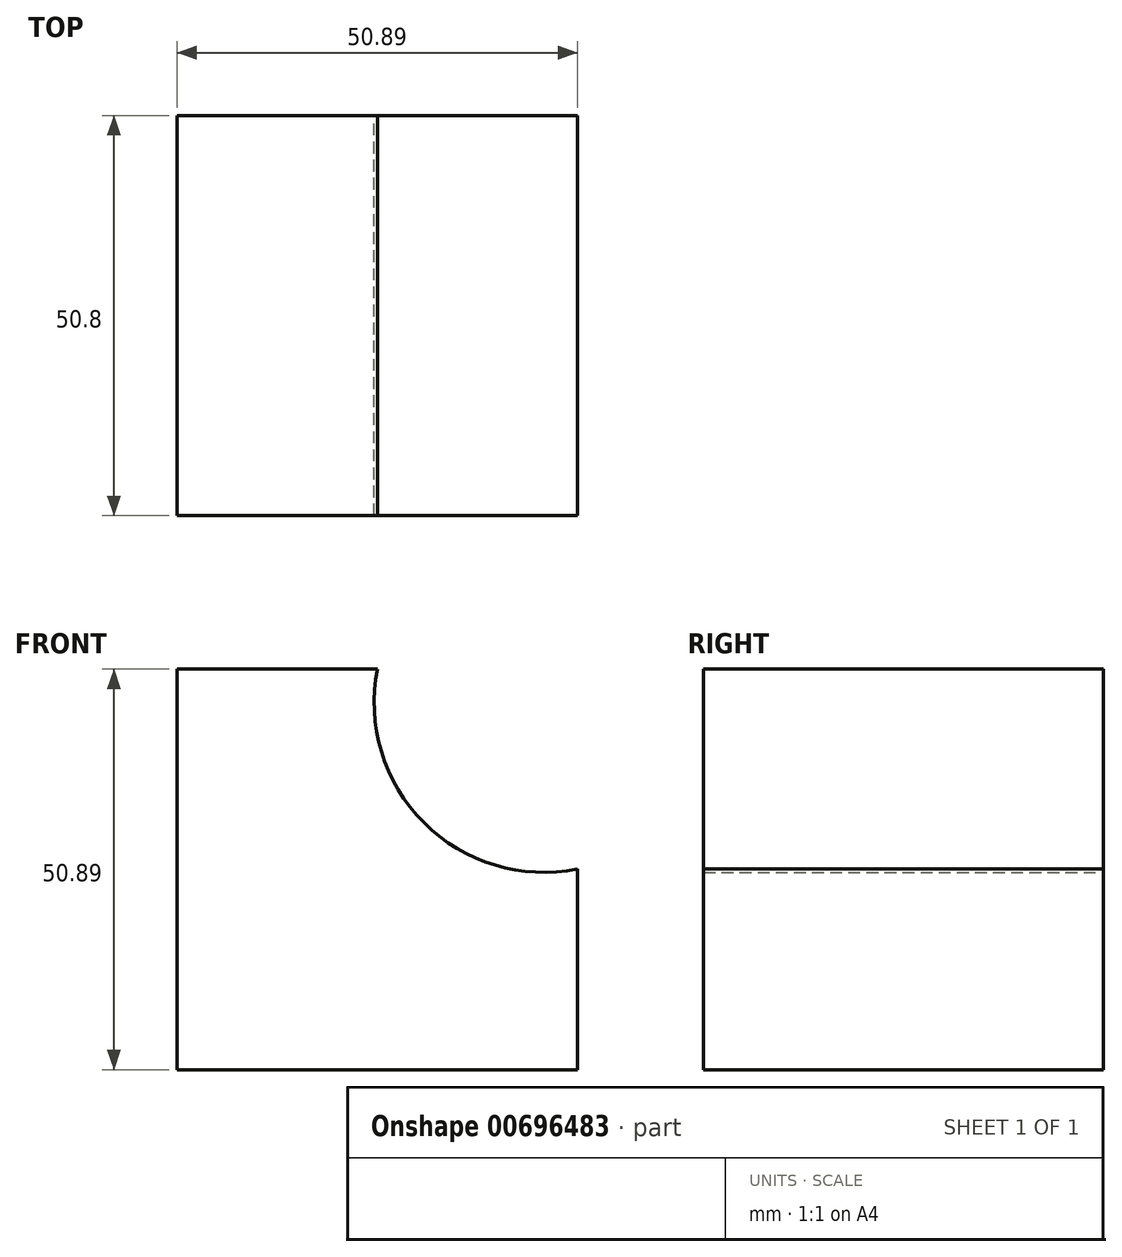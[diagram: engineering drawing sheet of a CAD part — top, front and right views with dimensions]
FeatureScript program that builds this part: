
annotation { "Feature Type Name" : "Feature", "Feature Type Description" : "" }
export const myFeature = defineFeature(function(context is Context, id is Id, definition is map)
    precondition{}
    {
        {
            var Q0;
            Q0=qCreatedBy(makeId("Front.planeOp"),FACE);
            var sketch = newSketch(context, id + "F0", { "sketchPlane" : qUnion([Q0])});
            skLineSegment(sketch, "E0", {"start": v(0, 0) * mm, "end": v(0, 50.89) * mm});
            skLineSegment(sketch, "E1", {"start": v(0, 50.89) * mm, "end": v(25.5, 50.89) * mm});
            skLineSegment(sketch, "E2", {"start": v(0, 0) * mm, "end": v(50.89, 0) * mm});
            skLineSegment(sketch, "E3", {"start": v(50.89, 0) * mm, "end": v(50.89, 25.5) * mm});
            skArc(sketch, "E4", {"start": v(25.5, 50.89) * mm, "mid": v(31.38, 31.38) * mm, "end": v(50.89, 25.5) * mm});
            skSolve(sketch);
        }
        {
            var Q0;
            Q0=makeQuery(id+"F0.imprint","IMPRINT",FACE,{"disambiguationData":[TD([[makeQuery(id+"F0.imprint","IMPRINT",EDGE,{"derivedFrom":sQuery(id+"F0.wireOp",EDGE,"E0")}),-1.0]])]});
            extrude(context, id + "F1", {"entities" : qUnion([Q0]), "depth" : 50.8 * mm, "offsetDistance" : 25.4 * mm});
        }
    });
